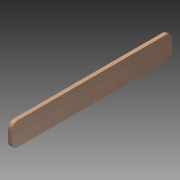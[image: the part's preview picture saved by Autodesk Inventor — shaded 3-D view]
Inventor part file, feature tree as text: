
AUTODESK INVENTOR PART (.ipt)
format: ipt  version: 2013 (Build 170138000, 138)  size: 90,112 bytes
history: native  units: in
note: dims shown in document units (in); Inventor stores cm internally (conversion verified against a paired STEP export)
features: extrude x1, fillet x1, sketch x1
ambient origin geometry x8: Origin, YZ Plane, XZ Plane, XY Plane, X Axis, Y Axis, Z Axis, Center Point
bodies: Solid1 (feature_tree)
feature tree (3):
  extrude  "Extrusion1"  Depth=0.75in
  fillet  "Fillet1"  Radius=34.5in
  sketch  "Sketch1"  dims[d0=5.0in d1=0.75in d2=34.5in d3=0.0in d4=1.3125in]
